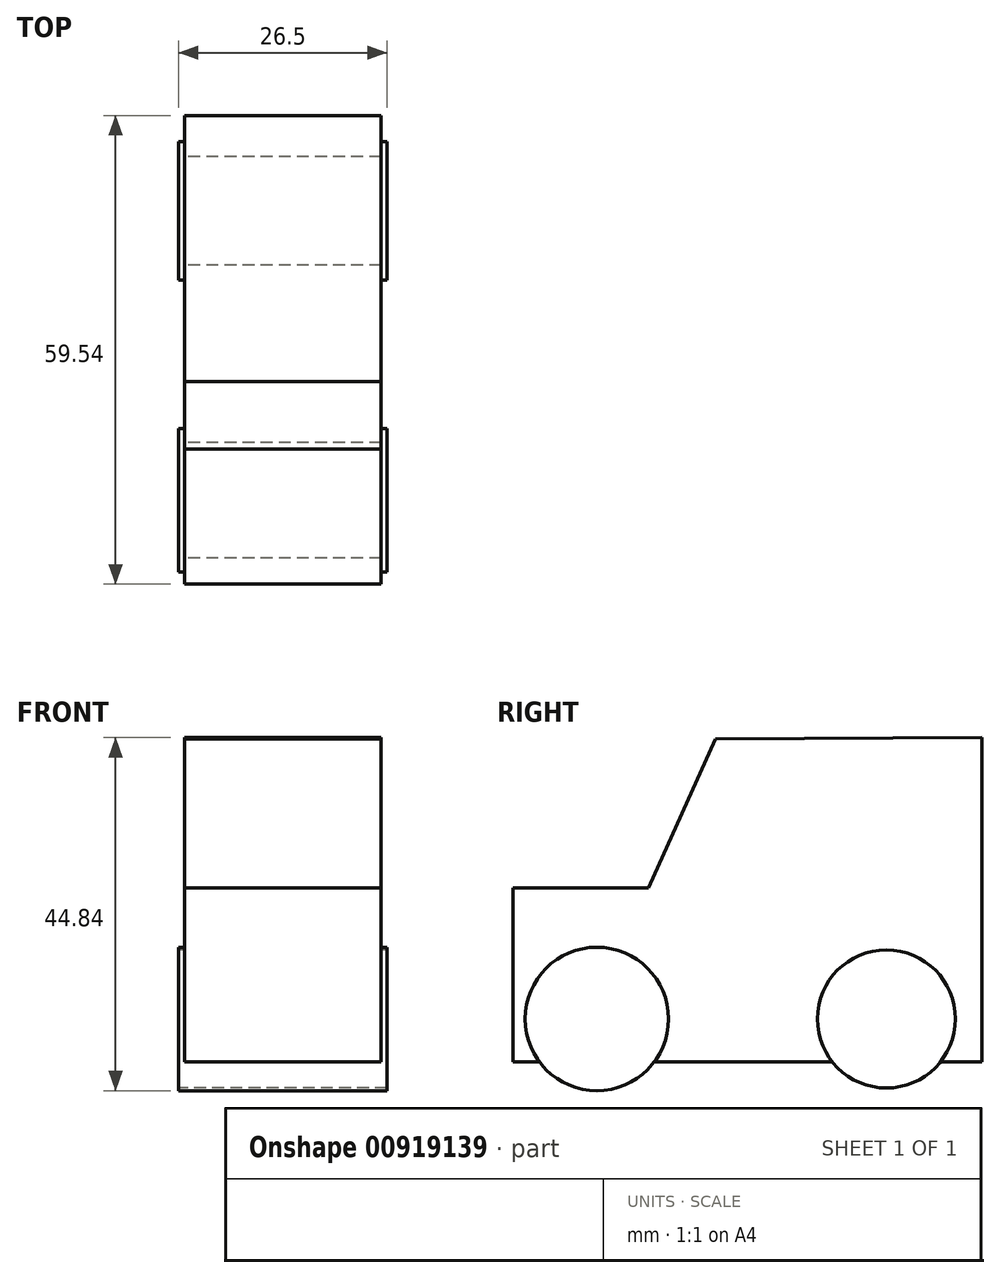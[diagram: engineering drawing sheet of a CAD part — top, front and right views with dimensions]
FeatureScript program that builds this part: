
annotation { "Feature Type Name" : "Feature", "Feature Type Description" : "" }
export const myFeature = defineFeature(function(context is Context, id is Id, definition is map)
    precondition{}
    {
        {
            var Q0;
            Q0=qCreatedBy(makeId("Right.planeOp"),FACE);
            var sketch = newSketch(context, id + "F0", { "sketchPlane" : qUnion([Q0])});
            skLineSegment(sketch, "E0", {"start": v(25.62, 26.98) * mm, "end": v(25.62, -14.18) * mm});
            skLineSegment(sketch, "E1", {"start": v(25.62, -14.18) * mm, "end": v(-33.92, -14.18) * mm});
            skLineSegment(sketch, "E2", {"start": v(-33.92, -14.18) * mm, "end": v(-33.92, 7.87) * mm});
            skLineSegment(sketch, "E3", {"start": v(-33.92, 7.87) * mm, "end": v(-16.72, 7.87) * mm});
            skLineSegment(sketch, "E4", {"start": v(-16.72, 7.87) * mm, "end": v(-8.2, 26.84) * mm});
            skLineSegment(sketch, "E5", {"start": v(-8.2, 26.84) * mm, "end": v(25.62, 26.98) * mm});
            skSolve(sketch);
        }
        {
            var Q0;
            Q0=makeQuery(id+"F0.imprint","IMPRINT",FACE,{"disambiguationData":[TD([[makeQuery(id+"F0.imprint","IMPRINT",EDGE,{"derivedFrom":sQuery(id+"F0.wireOp",EDGE,"E0")}),-1.0]])]});
            extrude(context, id + "F1", {"entities" : qUnion([Q0]), "depth" : 25 * mm, "offsetDistance" : 25 * mm, "symmetric" : true});
        }
        {
            var Q0;
            Q0=qCreatedBy(makeId("Right.planeOp"),FACE);
            var sketch = newSketch(context, id + "F2", { "sketchPlane" : qUnion([Q0])});
            skCircle(sketch, "E6", {"center": v(-23.27, -8.75) * mm, "radius": 9.11 * mm});
            skCircle(sketch, "E7", {"center": v(13.5, -8.75) * mm, "radius": 8.77 * mm});
            skSolve(sketch);
        }
        {
            var Q0;
            Q0 = qSketchRegion(id + "F2", true);
            extrude(context, id + "F3", {"entities" : qUnion([Q0]), "operationType" : NewBodyOperationType.ADD, "depth" : 26.5 * mm, "offsetDistance" : 25 * mm, "symmetric" : true});
        }
    });
